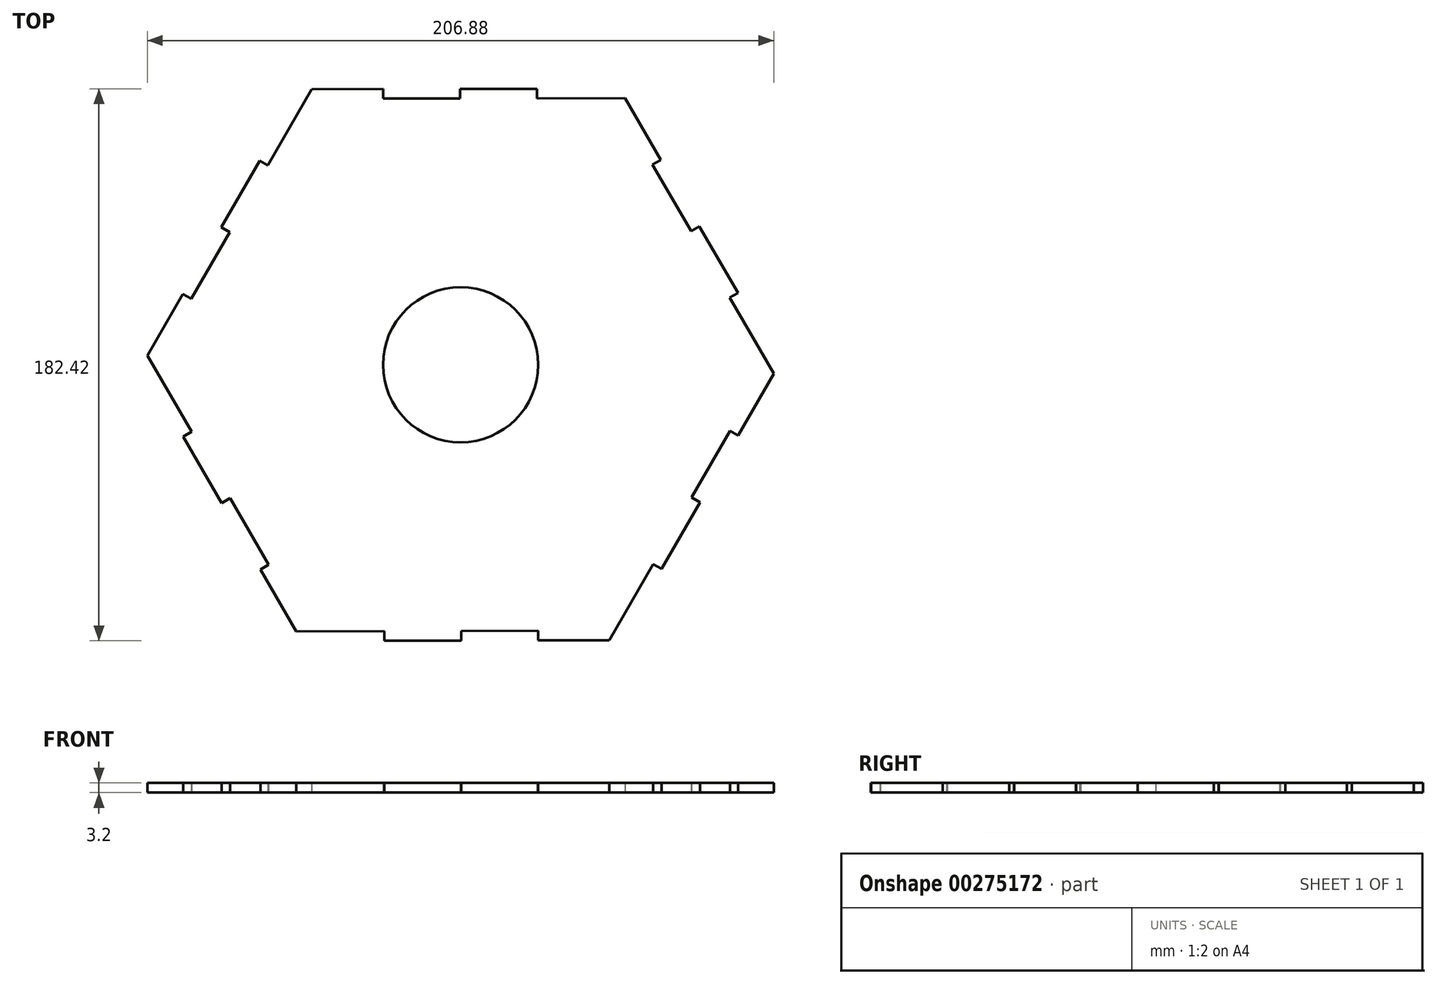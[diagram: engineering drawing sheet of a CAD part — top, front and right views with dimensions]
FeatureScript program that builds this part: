
annotation { "Feature Type Name" : "Feature", "Feature Type Description" : "" }
export const myFeature = defineFeature(function(context is Context, id is Id, definition is map)
    precondition{}
    {
        {
            var Q0;
            Q0=qCreatedBy(makeId("Top.planeOp"),FACE);
            var sketch = newSketch(context, id + "F0", { "sketchPlane" : qUnion([Q0])});
            skCircle(sketch, "E0.cCircle", {"center": v(0, 0) * mm, "radius": 87.99 * mm, "construction": true});
            skLineSegment(sketch, "E0.0", {"start": v(50.64, 88.08) * mm, "end": v(101.6, 0.19) * mm});
            skLineSegment(sketch, "E0.1", {"start": v(101.6, 0.19) * mm, "end": v(50.96, -87.9) * mm});
            skLineSegment(sketch, "E0.2", {"start": v(50.96, -87.9) * mm, "end": v(-50.64, -88.08) * mm});
            skLineSegment(sketch, "E0.3", {"start": v(-50.64, -88.08) * mm, "end": v(-101.6, -0.19) * mm});
            skLineSegment(sketch, "E0.4", {"start": v(-101.6, -0.19) * mm, "end": v(-50.96, 87.9) * mm});
            skLineSegment(sketch, "E0.5", {"start": v(-50.96, 87.9) * mm, "end": v(50.64, 88.08) * mm});
            skPoint(sketch, "E0.0.midPoint", {"position": v(76.12, 44.13) * mm});
            skLineSegment(sketch, "E1.0", {"start": v(-103.44, 2.99) * mm, "end": v(-47.12, 100.94) * mm, "construction": true});
            skLineSegment(sketch, "E2", {"start": v(-103.44, 2.99) * mm, "end": v(-91.7, 23.42) * mm});
            skLineSegment(sketch, "E3", {"start": v(-91.7, 23.42) * mm, "end": v(-88.94, 21.83) * mm});
            skLineSegment(sketch, "E4", {"start": v(-76.28, 43.85) * mm, "end": v(-79.03, 45.44) * mm});
            skLineSegment(sketch, "E5", {"start": v(-79.03, 45.44) * mm, "end": v(-66.37, 67.46) * mm});
            skLineSegment(sketch, "E6", {"start": v(-66.37, 67.46) * mm, "end": v(-63.62, 65.88) * mm});
            skLineSegment(sketch, "E7.1.0", {"start": v(-66.13, -67.7) * mm, "end": v(-63.38, -66.1) * mm});
            skLineSegment(sketch, "E7.1.1", {"start": v(-54.3, -88.09) * mm, "end": v(-66.13, -67.7) * mm});
            skLineSegment(sketch, "E7.1.3", {"start": v(-76.12, -44.13) * mm, "end": v(-78.87, -45.73) * mm});
            skLineSegment(sketch, "E7.1.4", {"start": v(-78.87, -45.73) * mm, "end": v(-91.6, -23.75) * mm});
            skLineSegment(sketch, "E7.1.5", {"start": v(-91.6, -23.75) * mm, "end": v(-88.86, -22.16) * mm});
            skLineSegment(sketch, "E7.2.0", {"start": v(25.57, -91.12) * mm, "end": v(25.56, -87.94) * mm});
            skLineSegment(sketch, "E7.2.1", {"start": v(49.13, -91.07) * mm, "end": v(25.57, -91.12) * mm});
            skLineSegment(sketch, "E7.2.3", {"start": v(0.16, -87.99) * mm, "end": v(0.17, -91.16) * mm});
            skLineSegment(sketch, "E7.2.4", {"start": v(0.17, -91.16) * mm, "end": v(-25.23, -91.2) * mm});
            skLineSegment(sketch, "E7.2.5", {"start": v(-25.23, -91.2) * mm, "end": v(-25.24, -88.03) * mm});
            skLineSegment(sketch, "E7.3.0", {"start": v(91.7, -23.42) * mm, "end": v(88.94, -21.83) * mm});
            skLineSegment(sketch, "E7.3.1", {"start": v(103.44, -2.99) * mm, "end": v(91.7, -23.42) * mm});
            skLineSegment(sketch, "E7.3.3", {"start": v(76.28, -43.85) * mm, "end": v(79.03, -45.44) * mm});
            skLineSegment(sketch, "E7.3.4", {"start": v(79.03, -45.44) * mm, "end": v(66.37, -67.46) * mm});
            skLineSegment(sketch, "E7.3.5", {"start": v(66.37, -67.46) * mm, "end": v(63.62, -65.88) * mm});
            skLineSegment(sketch, "E7.4.0", {"start": v(66.13, 67.7) * mm, "end": v(63.38, 66.1) * mm});
            skLineSegment(sketch, "E7.4.1", {"start": v(54.3, 88.09) * mm, "end": v(66.13, 67.7) * mm});
            skLineSegment(sketch, "E7.4.3", {"start": v(76.12, 44.13) * mm, "end": v(78.87, 45.73) * mm});
            skLineSegment(sketch, "E7.4.4", {"start": v(78.87, 45.73) * mm, "end": v(91.6, 23.75) * mm});
            skLineSegment(sketch, "E7.4.5", {"start": v(91.6, 23.75) * mm, "end": v(88.86, 22.16) * mm});
            skLineSegment(sketch, "E7.5.0", {"start": v(-25.57, 91.12) * mm, "end": v(-25.56, 87.94) * mm});
            skLineSegment(sketch, "E7.5.1", {"start": v(-49.13, 91.07) * mm, "end": v(-25.57, 91.12) * mm});
            skLineSegment(sketch, "E7.5.3", {"start": v(-0.16, 87.99) * mm, "end": v(-0.17, 91.16) * mm});
            skLineSegment(sketch, "E7.5.4", {"start": v(-0.17, 91.16) * mm, "end": v(25.23, 91.2) * mm});
            skLineSegment(sketch, "E7.5.5", {"start": v(25.23, 91.2) * mm, "end": v(25.24, 88.03) * mm});
            skLineSegment(sketch, "E8", {"start": v(-101.6, -0.19) * mm, "end": v(-103.44, 2.99) * mm});
            skPoint(sketch, "E9.orphan", {"position": v(-104.35, 1.4) * mm});
            skLineSegment(sketch, "E10.1.0", {"start": v(-50.64, -88.08) * mm, "end": v(-54.3, -88.09) * mm});
            skLineSegment(sketch, "E10.2.0", {"start": v(50.96, -87.9) * mm, "end": v(49.13, -91.07) * mm});
            skLineSegment(sketch, "E10.3.0", {"start": v(101.6, 0.19) * mm, "end": v(103.44, -2.99) * mm});
            skLineSegment(sketch, "E10.4.0", {"start": v(50.64, 88.08) * mm, "end": v(54.3, 88.09) * mm});
            skLineSegment(sketch, "E10.5.0", {"start": v(-50.96, 87.9) * mm, "end": v(-49.13, 91.07) * mm});
            skPoint(sketch, "E11.orphan", {"position": v(-50.97, 91.07) * mm});
            skPoint(sketch, "E12.orphan", {"position": v(104.35, -1.4) * mm});
            skPoint(sketch, "E13.orphan", {"position": v(50.97, -91.07) * mm});
            skPoint(sketch, "E14.orphan", {"position": v(-53.39, -89.67) * mm});
            skSolve(sketch);
        }
        {
            var Q0;
            {var subQ18=sQuery(id+"F0.wireOp",EDGE,"E0.0");var subQ26=makeQuery(id+"F0.imprint","INTERSECT",VERTEX,{"derivedFrom":[subQ18,sQuery(id+"F0.wireOp",EDGE,"E7.4.0")]});Q0=makeQuery(id+"F0.imprint","IMPRINT",FACE,{"disambiguationData":[TD([[makeQuery(id+"F0.imprint","IMPRINT",EDGE,{"disambiguationData":[TD([[subQ26,-1.0]])],"derivedFrom":subQ18}),-1.0]])]});}
            var Q1;
            {var subQ0=sQuery(id+"F0.wireOp",EDGE,"E4");Q1=makeQuery(id+"F0.imprint","IMPRINT",FACE,{"disambiguationData":[TD([[makeQuery(id+"F0.imprint","IMPRINT",EDGE,{"derivedFrom":subQ0}),-1.0]])]});}
            var Q2;
            Q2=makeQuery(id+"F0.imprint","IMPRINT",FACE,{"disambiguationData":[TD([[makeQuery(id+"F0.imprint","IMPRINT",EDGE,{"derivedFrom":sQuery(id+"F0.wireOp",EDGE,"E2")}),-1.0]])]});
            var Q3;
            {var subQ2=sQuery(id+"F0.wireOp",EDGE,"E7.5.0");Q3=makeQuery(id+"F0.imprint","IMPRINT",FACE,{"disambiguationData":[TD([[makeQuery(id+"F0.imprint","IMPRINT",EDGE,{"derivedFrom":subQ2}),-1.0]])]});}
            var Q4;
            {var subQ0=sQuery(id+"F0.wireOp",EDGE,"E7.5.3");Q4=makeQuery(id+"F0.imprint","IMPRINT",FACE,{"disambiguationData":[TD([[makeQuery(id+"F0.imprint","IMPRINT",EDGE,{"derivedFrom":subQ0}),-1.0]])]});}
            var Q5;
            {var subQ2=sQuery(id+"F0.wireOp",EDGE,"E7.4.0");Q5=makeQuery(id+"F0.imprint","IMPRINT",FACE,{"disambiguationData":[TD([[makeQuery(id+"F0.imprint","IMPRINT",EDGE,{"derivedFrom":subQ2}),-1.0]])]});}
            var Q6;
            {var subQ0=sQuery(id+"F0.wireOp",EDGE,"E7.4.3");Q6=makeQuery(id+"F0.imprint","IMPRINT",FACE,{"disambiguationData":[TD([[makeQuery(id+"F0.imprint","IMPRINT",EDGE,{"derivedFrom":subQ0}),-1.0]])]});}
            var Q7;
            {var subQ2=sQuery(id+"F0.wireOp",EDGE,"E7.3.0");Q7=makeQuery(id+"F0.imprint","IMPRINT",FACE,{"disambiguationData":[TD([[makeQuery(id+"F0.imprint","IMPRINT",EDGE,{"derivedFrom":subQ2}),-1.0]])]});}
            var Q8;
            {var subQ0=sQuery(id+"F0.wireOp",EDGE,"E7.3.3");Q8=makeQuery(id+"F0.imprint","IMPRINT",FACE,{"disambiguationData":[TD([[makeQuery(id+"F0.imprint","IMPRINT",EDGE,{"derivedFrom":subQ0}),-1.0]])]});}
            var Q9;
            {var subQ2=sQuery(id+"F0.wireOp",EDGE,"E7.2.0");Q9=makeQuery(id+"F0.imprint","IMPRINT",FACE,{"disambiguationData":[TD([[makeQuery(id+"F0.imprint","IMPRINT",EDGE,{"derivedFrom":subQ2}),-1.0]])]});}
            var Q10;
            {var subQ0=sQuery(id+"F0.wireOp",EDGE,"E7.2.3");Q10=makeQuery(id+"F0.imprint","IMPRINT",FACE,{"disambiguationData":[TD([[makeQuery(id+"F0.imprint","IMPRINT",EDGE,{"derivedFrom":subQ0}),-1.0]])]});}
            var Q11;
            {var subQ2=sQuery(id+"F0.wireOp",EDGE,"E7.1.0");Q11=makeQuery(id+"F0.imprint","IMPRINT",FACE,{"disambiguationData":[TD([[makeQuery(id+"F0.imprint","IMPRINT",EDGE,{"derivedFrom":subQ2}),-1.0]])]});}
            var Q12;
            {var subQ0=sQuery(id+"F0.wireOp",EDGE,"E7.1.3");Q12=makeQuery(id+"F0.imprint","IMPRINT",FACE,{"disambiguationData":[TD([[makeQuery(id+"F0.imprint","IMPRINT",EDGE,{"derivedFrom":subQ0}),-1.0]])]});}
            extrude(context, id + "F1", {"entities" : qUnion([Q0, Q1, Q2, Q3, Q4, Q5, Q6, Q7, Q8, Q9, Q10, Q11, Q12]), "depth" : 3.17 * mm});
        }
        {
            var Q0;
            Q0=makeQuery(id+"F1.opExtrude","CAP_FACE",FACE,{"disambiguationData":[OSD([sQuery(id+"F0.wireOp",EDGE,"E0.0"),sQuery(id+"F0.wireOp",EDGE,"E0.1"),sQuery(id+"F0.wireOp",EDGE,"E0.2"),sQuery(id+"F0.wireOp",EDGE,"E0.3"),sQuery(id+"F0.wireOp",EDGE,"E0.4"),sQuery(id+"F0.wireOp",EDGE,"E0.5"),sQuery(id+"F0.wireOp",EDGE,"E2"),sQuery(id+"F0.wireOp",EDGE,"E3"),sQuery(id+"F0.wireOp",EDGE,"E4"),sQuery(id+"F0.wireOp",EDGE,"E5"),sQuery(id+"F0.wireOp",EDGE,"E6"),sQuery(id+"F0.wireOp",EDGE,"E7.1.0"),sQuery(id+"F0.wireOp",EDGE,"E7.1.1"),sQuery(id+"F0.wireOp",EDGE,"E7.1.3"),sQuery(id+"F0.wireOp",EDGE,"E7.1.4"),sQuery(id+"F0.wireOp",EDGE,"E7.1.5"),sQuery(id+"F0.wireOp",EDGE,"E7.2.0"),sQuery(id+"F0.wireOp",EDGE,"E7.2.1"),sQuery(id+"F0.wireOp",EDGE,"E7.2.3"),sQuery(id+"F0.wireOp",EDGE,"E7.2.4"),sQuery(id+"F0.wireOp",EDGE,"E7.2.5"),sQuery(id+"F0.wireOp",EDGE,"E7.3.0"),sQuery(id+"F0.wireOp",EDGE,"E7.3.1"),sQuery(id+"F0.wireOp",EDGE,"E7.3.3"),sQuery(id+"F0.wireOp",EDGE,"E7.3.4"),sQuery(id+"F0.wireOp",EDGE,"E7.3.5"),sQuery(id+"F0.wireOp",EDGE,"E7.4.0"),sQuery(id+"F0.wireOp",EDGE,"E7.4.1"),sQuery(id+"F0.wireOp",EDGE,"E7.4.3"),sQuery(id+"F0.wireOp",EDGE,"E7.4.4"),sQuery(id+"F0.wireOp",EDGE,"E7.4.5"),sQuery(id+"F0.wireOp",EDGE,"E7.5.0"),sQuery(id+"F0.wireOp",EDGE,"E7.5.1"),sQuery(id+"F0.wireOp",EDGE,"E7.5.3"),sQuery(id+"F0.wireOp",EDGE,"E7.5.4"),sQuery(id+"F0.wireOp",EDGE,"E7.5.5"),sQuery(id+"F0.wireOp",EDGE,"E8"),sQuery(id+"F0.wireOp",EDGE,"E10.1.0"),sQuery(id+"F0.wireOp",EDGE,"E10.2.0"),sQuery(id+"F0.wireOp",EDGE,"E10.3.0"),sQuery(id+"F0.wireOp",EDGE,"E10.4.0"),sQuery(id+"F0.wireOp",EDGE,"E10.5.0")])],"isStart":false});
            var sketch = newSketch(context, id + "F2", { "sketchPlane" : qUnion([Q0])});
            skCircle(sketch, "E15", {"center": v(0, 0) * mm, "radius": 25.62 * mm});
            skSolve(sketch);
        }
        {
            var Q0;
            Q0=makeQuery(id+"F2.imprint","IMPRINT",FACE,{"disambiguationData":[TD([[makeQuery(id+"F2.imprint","IMPRINT",EDGE,{"derivedFrom":sQuery(id+"F2.wireOp",EDGE,"E15")}),1.0]])]});
            extrude(context, id + "F3", {"entities" : qUnion([Q0]), "operationType" : NewBodyOperationType.ADD, "depth" : 0.03 * mm});
        }
    });
